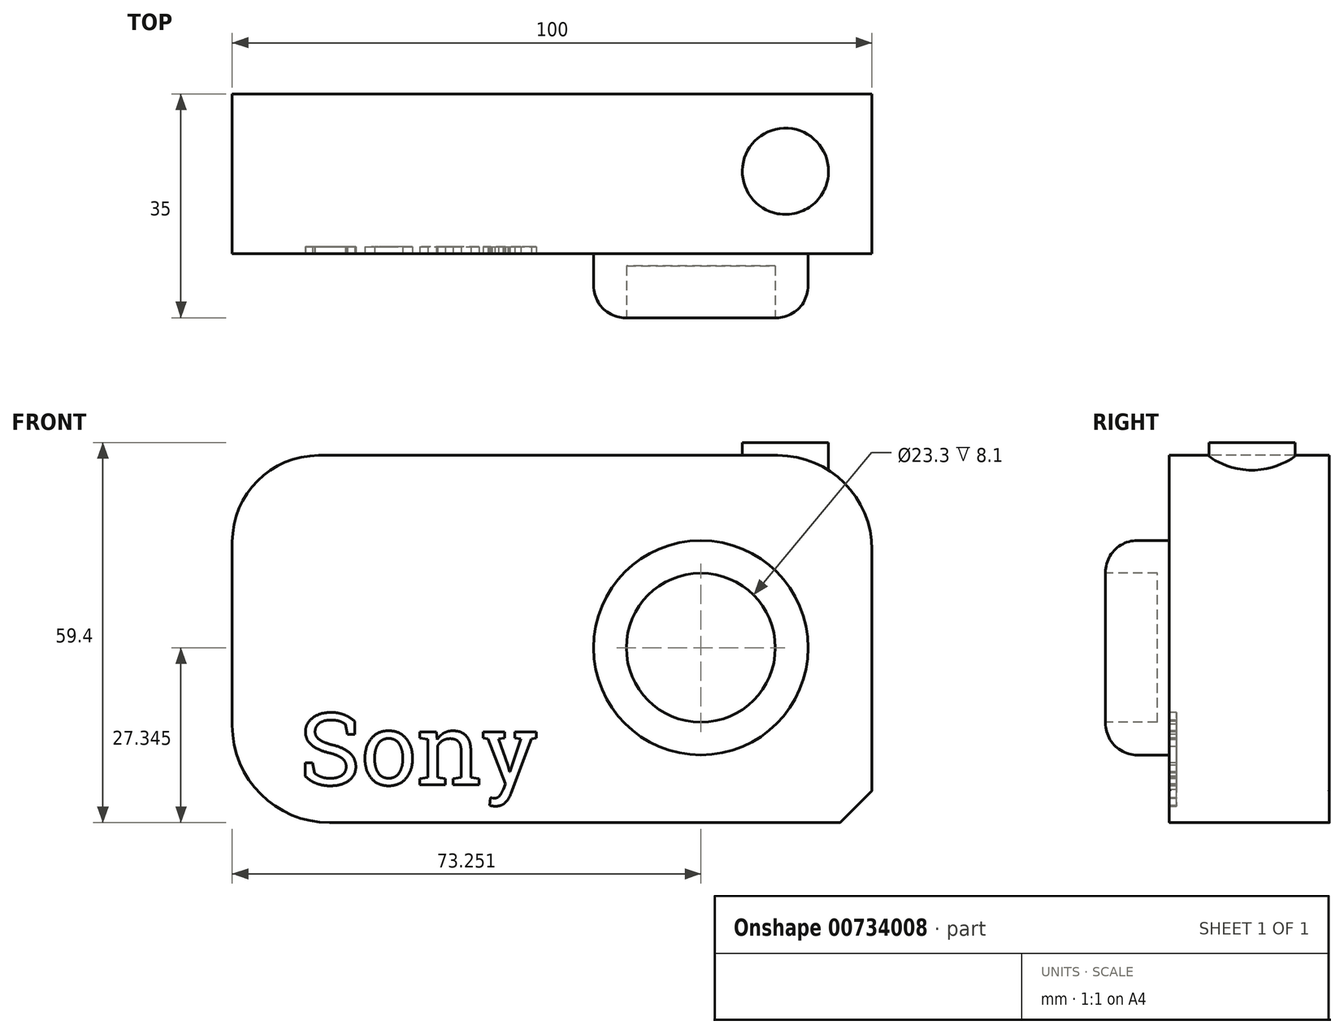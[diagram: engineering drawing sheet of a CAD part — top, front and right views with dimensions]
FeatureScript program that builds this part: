
annotation { "Feature Type Name" : "Feature", "Feature Type Description" : "" }
export const myFeature = defineFeature(function(context is Context, id is Id, definition is map)
    precondition{}
    {
        {
            var Q0;
            Q0=qCreatedBy(makeId("Top.planeOp"),FACE);
            var sketch = newSketch(context, id + "F0", { "sketchPlane" : qUnion([Q0])});
            skLineSegment(sketch, "E0.bottom", {"start": v(-108.64, -19.32) * mm, "end": v(-8.64, -19.32) * mm});
            skLineSegment(sketch, "E0.top", {"start": v(-108.64, -44.32) * mm, "end": v(-8.64, -44.32) * mm});
            skLineSegment(sketch, "E0.left", {"start": v(-108.64, -19.32) * mm, "end": v(-108.64, -44.32) * mm});
            skLineSegment(sketch, "E0.right", {"start": v(-8.64, -19.32) * mm, "end": v(-8.64, -44.32) * mm});
            skSolve(sketch);
        }
        {
            var Q0;
            Q0=qSketchRegion(id+"F0",true);
            extrude(context, id + "F1", {"entities" : qUnion([Q0]), "depth" : 57.4 * mm, "offsetDistance" : 25 * mm});
        }
        {
            var Q0;
            Q0=makeQuery(id+"F1.opExtrude","SWEPT_FACE",FACE,{"disambiguationData":[OSD([sQuery(id+"F0.wireOp",EDGE,"E0.top")])]});
            var sketch = newSketch(context, id + "F2", { "sketchPlane" : qUnion([Q0])});
            skCircle(sketch, "E1", {"center": v(-35.39, 27.34) * mm, "radius": 16.76 * mm});
            skSolve(sketch);
        }
        {
            var Q0;
            Q0=qSketchRegion(id+"F2",true);
            extrude(context, id + "F3", {"entities" : qUnion([Q0]), "operationType" : NewBodyOperationType.ADD, "depth" : 10 * mm, "offsetDistance" : 25 * mm});
        }
        {
            var Q0;
            Q0=makeQuery(id+"F3.opExtrude","CAP_FACE",FACE,{"disambiguationData":[OSD([sQuery(id+"F2.wireOp",EDGE,"E1")])],"isStart":false});
            var sketch = newSketch(context, id + "F4", { "sketchPlane" : qUnion([Q0])});
            skCircle(sketch, "E2", {"center": v(-35.39, 27.34) * mm, "radius": 11.65 * mm});
            skSolve(sketch);
        }
        {
            var Q0;
            Q0=qSketchRegion(id+"F4",true);
            extrude(context, id + "F5", {"entities" : qUnion([Q0]), "operationType" : NewBodyOperationType.REMOVE, "oppositeDirection" : true, "depth" : 8.1 * mm, "offsetDistance" : 25 * mm});
        }
        {
            var Q0;
            Q0=makeQuery(id+"F1.opExtrude","CAP_EDGE",EDGE,{"disambiguationData":[OSD([sQuery(id+"F0.wireOp",EDGE,"E0.left")])],"isStart":false});
            fillet(context, id + "F6", {"entities" : qUnion([Q0]), "radius" : 13.52 * mm, "tangentPropagation" : true, "allowEdgeOverflow" : false});
        }
        {
            var Q0;
            Q0=makeQuery(id+"F1.opExtrude","CAP_EDGE",EDGE,{"disambiguationData":[OSD([sQuery(id+"F0.wireOp",EDGE,"E0.right")])],"isStart":true});
            chamfer(context, id + "F7", {"entities" : qUnion([Q0]), "width" : 5 * mm, "tangentPropagation" : true});
        }
        {
            var Q0;
            Q0=makeQuery(id+"F3.opExtrude","CAP_EDGE",EDGE,{"disambiguationData":[OSD([sQuery(id+"F2.wireOp",EDGE,"E1")])],"isStart":false});
            fillet(context, id + "F8", {"entities" : qUnion([Q0]), "radius" : 5 * mm, "tangentPropagation" : true, "allowEdgeOverflow" : false});
        }
        {
            var Q0;
            Q0=makeQuery(id+"F1.opExtrude","CAP_FACE",FACE,{"disambiguationData":[OSD([sQuery(id+"F0.wireOp",EDGE,"E0.bottom"),sQuery(id+"F0.wireOp",EDGE,"E0.top"),sQuery(id+"F0.wireOp",EDGE,"E0.left"),sQuery(id+"F0.wireOp",EDGE,"E0.right")])],"isStart":false});
            var sketch = newSketch(context, id + "F9", { "sketchPlane" : qUnion([Q0])});
            skCircle(sketch, "E3", {"center": v(-22.17, -31.42) * mm, "radius": 6.73 * mm});
            skSolve(sketch);
        }
        {
            var Q0;
            Q0=qSketchRegion(id+"F9",true);
            extrude(context, id + "F10", {"entities" : qUnion([Q0]), "operationType" : NewBodyOperationType.ADD, "depth" : 2 * mm, "offsetDistance" : 25 * mm});
        }
        {
            var Q0;
            Q0=makeQuery(id+"F1.opExtrude","SWEPT_FACE",FACE,{"disambiguationData":[OSD([sQuery(id+"F0.wireOp",EDGE,"E0.top")])]});
            var sketch = newSketch(context, id + "F11", { "sketchPlane" : qUnion([Q0])});
            skText(sketch, "E4", { "text": "Sony", "fontName": "RobotoSlab-Regular.ttf"});
            const initialGuessF11  = {"E4": [-0.09814, 0.00592, 1, 0, 0.0113]};
            skSetInitialGuess(sketch, initialGuessF11);
            skSolve(sketch);
        }
        {
            var Q0;
            Q0=qSketchRegion(id+"F11",true);
            extrude(context, id + "F12", {"entities" : qUnion([Q0]), "operationType" : NewBodyOperationType.REMOVE, "oppositeDirection" : true, "depth" : 1.1 * mm, "offsetDistance" : 25 * mm});
        }
        {
            var Q0;
            Q0=makeQuery(id+"F1.opExtrude","CAP_EDGE",EDGE,{"disambiguationData":[OSD([sQuery(id+"F0.wireOp",EDGE,"E0.right")])],"isStart":false});
            fillet(context, id + "F13", {"entities" : qUnion([Q0]), "radius" : 14.73 * mm, "tangentPropagation" : true, "allowEdgeOverflow" : false});
        }
        {
            var Q0;
            Q0=makeQuery(id+"F7.opChamfer","BLEND_FACE",FACE,{"disambiguationData":[OSD([sQuery(id+"F0.wireOp",EDGE,"E0.right")])]});
            fillet(context, id + "F14", {"entities" : qUnion([Q0]), "radius" : 0.12 * mm, "tangentPropagation" : true, "allowEdgeOverflow" : false});
        }
        {
            var Q0;
            Q0=makeQuery(id+"F1.opExtrude","CAP_EDGE",EDGE,{"disambiguationData":[OSD([sQuery(id+"F0.wireOp",EDGE,"E0.left")])],"isStart":true});
            fillet(context, id + "F15", {"entities" : qUnion([Q0]), "radius" : 15.2 * mm, "tangentPropagation" : true, "allowEdgeOverflow" : false});
        }
    });
